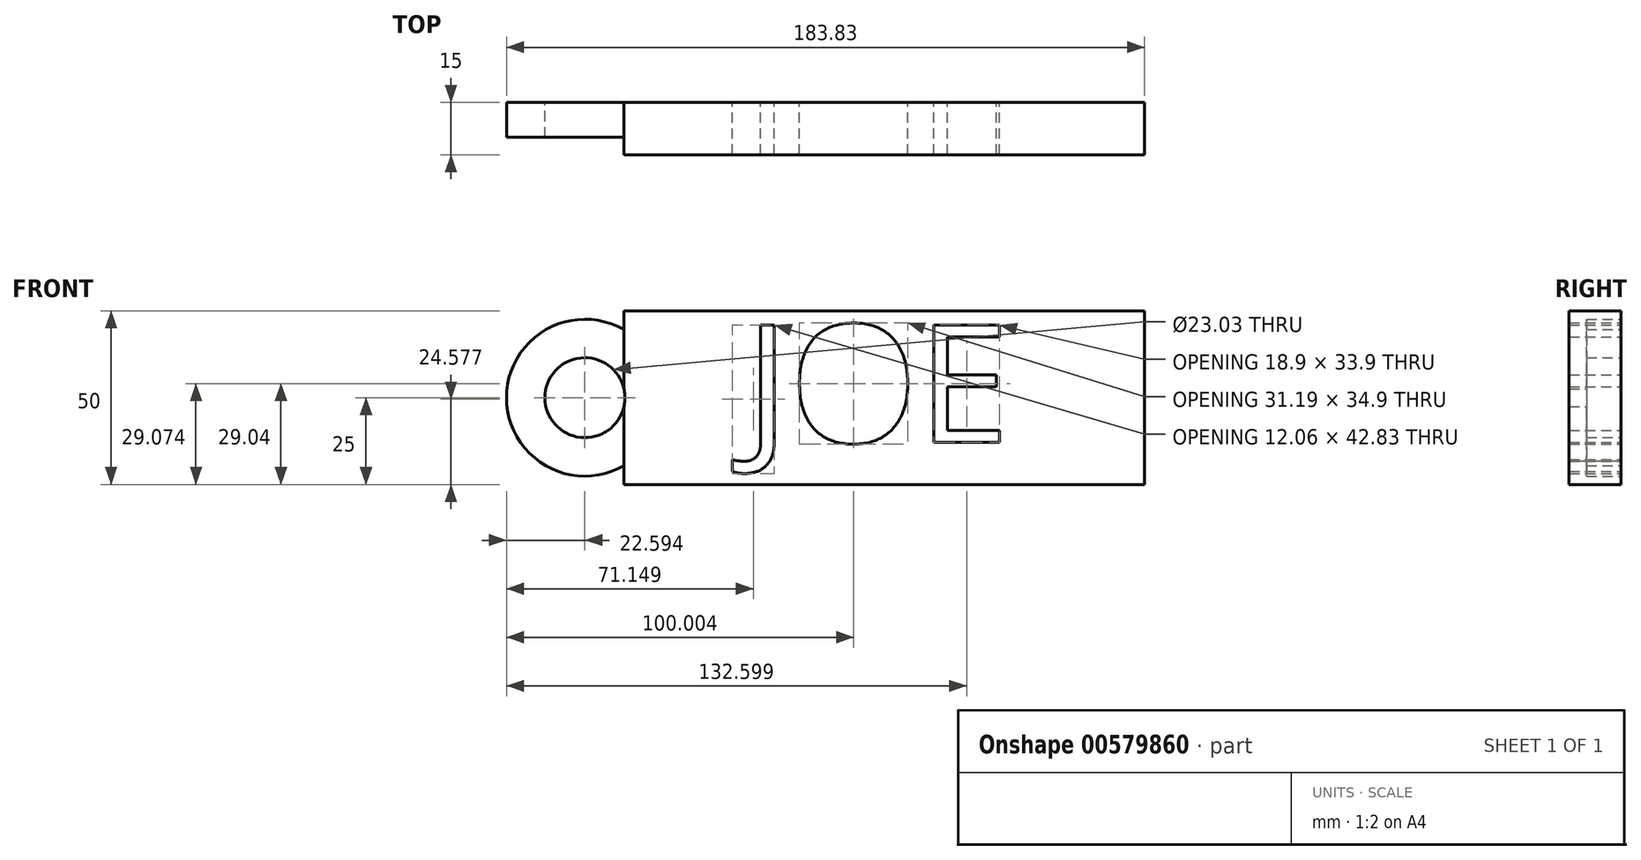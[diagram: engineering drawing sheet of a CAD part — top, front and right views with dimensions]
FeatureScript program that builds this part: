
annotation { "Feature Type Name" : "Feature", "Feature Type Description" : "" }
export const myFeature = defineFeature(function(context is Context, id is Id, definition is map)
    precondition{}
    {
        {
            var Q0;
            Q0=qCreatedBy(makeId("Front.planeOp"),FACE);
            var sketch = newSketch(context, id + "F0", { "sketchPlane" : qUnion([Q0])});
            skLineSegment(sketch, "E0", {"start": v(0, 0) * mm, "end": v(-150, 0) * mm});
            skLineSegment(sketch, "E1", {"start": v(-150, 0) * mm, "end": v(-150, 50) * mm});
            skLineSegment(sketch, "E2", {"start": v(-150, 50) * mm, "end": v(0, 50) * mm});
            skLineSegment(sketch, "E3", {"start": v(0, 50) * mm, "end": v(0, 0) * mm});
            skArc(sketch, "E4", {"start": v(-150, 44.6) * mm, "mid": v(-183.83, 25) * mm, "end": v(-150, 5.4) * mm});
            skCircle(sketch, "E5", {"center": v(-161.24, 25) * mm, "radius": 11.52 * mm});
            skLineSegment(sketch, "E6", {"start": v(-161.24, 25) * mm, "end": v(0, 25) * mm, "construction": true});
            skText(sketch, "E7", { "text": "JOE", "fontName": "OpenSans-Regular.ttf"});
            skLineSegment(sketch, "E8", {"start": v(-75, 12.09) * mm, "end": v(-75, 0) * mm, "construction": true});
            const initialGuessF0  = {"E7": [-0.115, 0.01209, 1, 0, 0.03419]};
            skSetInitialGuess(sketch, initialGuessF0);
            skSolve(sketch);
        }
        {
            var Q0;
            {var subQ7=sQuery(id+"F0.wireOp",EDGE,"E0");Q0=makeQuery(id+"F0.imprint","IMPRINT",FACE,{"disambiguationData":[TD([[makeQuery(id+"F0.imprint","IMPRINT",EDGE,{"derivedFrom":subQ7}),-1.0]])]});}
            extrude(context, id + "F1", {"entities" : qUnion([Q0]), "depth" : 15 * mm, "offsetDistance" : 25 * mm});
        }
        {
            var Q0;
            {var subQ0=sQuery(id+"F0.wireOp",EDGE,"E4");Q0=makeQuery(id+"F0.imprint","IMPRINT",FACE,{"disambiguationData":[TD([[makeQuery(id+"F0.imprint","IMPRINT",EDGE,{"derivedFrom":subQ0}),1.0]])]});}
            extrude(context, id + "F2", {"entities" : qUnion([Q0]), "operationType" : NewBodyOperationType.ADD, "depth" : 10 * mm, "offsetDistance" : 25 * mm});
        }
    });
